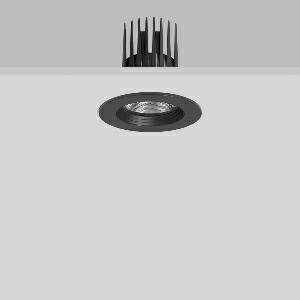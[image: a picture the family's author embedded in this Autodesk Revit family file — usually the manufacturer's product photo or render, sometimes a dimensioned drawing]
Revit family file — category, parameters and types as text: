
# Revit family: heledon_mini_e_901740_003_76_393d
name_source: partatom
category: Lighting Fixtures
units: mm (PartAtom-declared; Revit-internal decimal feet)

## family parameters
Cut with Voids When Loaded = No
Host = Face
Light Source = No
Part Type = Normal
Room Calculation Point = No
Round Connector Dimension = Use Diameter
Shared = No

## types (1)
- HELEDON mini E (1 x LED Modul 930, 2500 lm, 3000)
    Apparent Load = 20 VA
    Approval mark = CE
    CIE Flux Codes = 100 100 100 100 100
    Color Rendering = 90
    Color Temperature = 3000
    Default Elevation = 1800 mm
    Description = Series: HELEDON mini
Round recessed downlight. Housing: die-cast aluminium, powder-coated. Black plastic ring and recessed LED to prevent glare from the side. Optical assembly with reflector made of MIRO-Silver with 98% total light reflection for outstanding efficiency - can be changed without tools. Best colour rendering index Ra>90. Suitable for Recessed ceiling mounting. Installation without tools thanks to spring fastening system. Including separate LED converter with connecting cable 600 mm.High quality converter without flickering and stroboscopic effect. Through-wiring box (5 pole) available as accessory. The following accessories can be mounted without use of tools: interchangeable lenses, decorative glasses, honeycomb louvre, clear and frosted diffusers, white interchangeable plastic ring. 
Colour: deep black, matt (RAL 9005)
Diameter: 124 mm
Height: 3 mm
Cut-out diameter: 114 mm
Recess height: 170 mm
Luminaire: recess height: 120 mm
Lamp: LED
Socket: without socket
Colour temperature: 3000K
Colour rendering index (CRI): 92
System power: 20 W
Rated luminous flux: 2500 lm
Luminous efficiency: 125 lm/W
Control gear: Converter, dimmable, DALI
Protection class: II
Type of protection: IP 20
    Height = 0 mm  [stored 0 ft]
    Lamp = 1 x LED Modul 930
    Lamp Light Flux = 2500 lm
    Lamp count = 1
    Length = 124 mm  [stored 0.406824 ft]
    Lifetime = 50000 h
    Luminous efficacy = 125 lm/W
    Manufacturer = RZB
    ModVariant = No
    Model = 901740.003.76
    Mounting Place = Ceiling
    Mounting Type = Recessed
    Number of Poles = 1
    OnlyDefault = Yes
    Power Factor = 1
    Product Name = HELEDON mini E
    Product group = Recessed downlights
    ProductGroupID = 402
    Protection Class = Protection class II
    Protection Degree = IP 20
    RLX_Detail_Level = 1
    RLX_Emergency_Light_Flux = 0 lm
    RLX_Emergency_Type = 0
    RLX_Emergency_Type_DB = No
    RlxData = <blob elided: 127413 chars, md5=55132661>
    Socket = socket
    Standby Power = 0 W
    System Light Flux = 2500 lm
    System Power = 20 W
    Type Comments = Product without accessories
    Type Image = 901657.003.jpg
    URL = http://relux.com
    VarID = ---
    Voltage = 230 V
    Voltage Range = 220-240 V
    Weight = 0.00 kg
    Width = 0 mm  [stored 0 ft]

note: [stored X ft] marks values corroborated as IEEE doubles in the binary element streams (Revit-internal decimal feet)

## geometry (parser evidence)
native form markers: Blend x4, Sweep x13
no freeform markers — native parametric forms only
